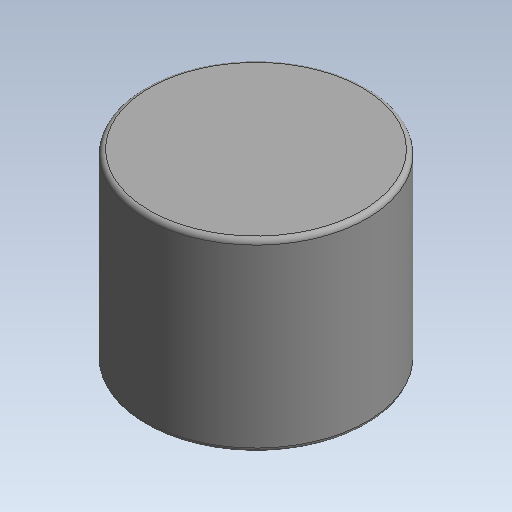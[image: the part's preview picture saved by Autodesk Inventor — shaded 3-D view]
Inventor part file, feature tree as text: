
AUTODESK INVENTOR PART (.ipt)
format: ipt  version: 2020 (Build 240168000, 168)  size: 69,120 bytes
history: native  units: mm (DEFAULTED — no unit token found)
features: fillet x1
ambient origin geometry x8: Origin, YZ Plane, XZ Plane, XY Plane, X Axis, Y Axis, Z Axis, Center Point
bodies: Solid1 (feature_tree)
feature tree (1):
  fillet  "Fillet1"  [1 undecoded]
note: 1 required parameter value undecoded (feature->parameter linkage not recoverable at this tier; creation-order binding heuristic only, values carry confidence <= 0.55)
